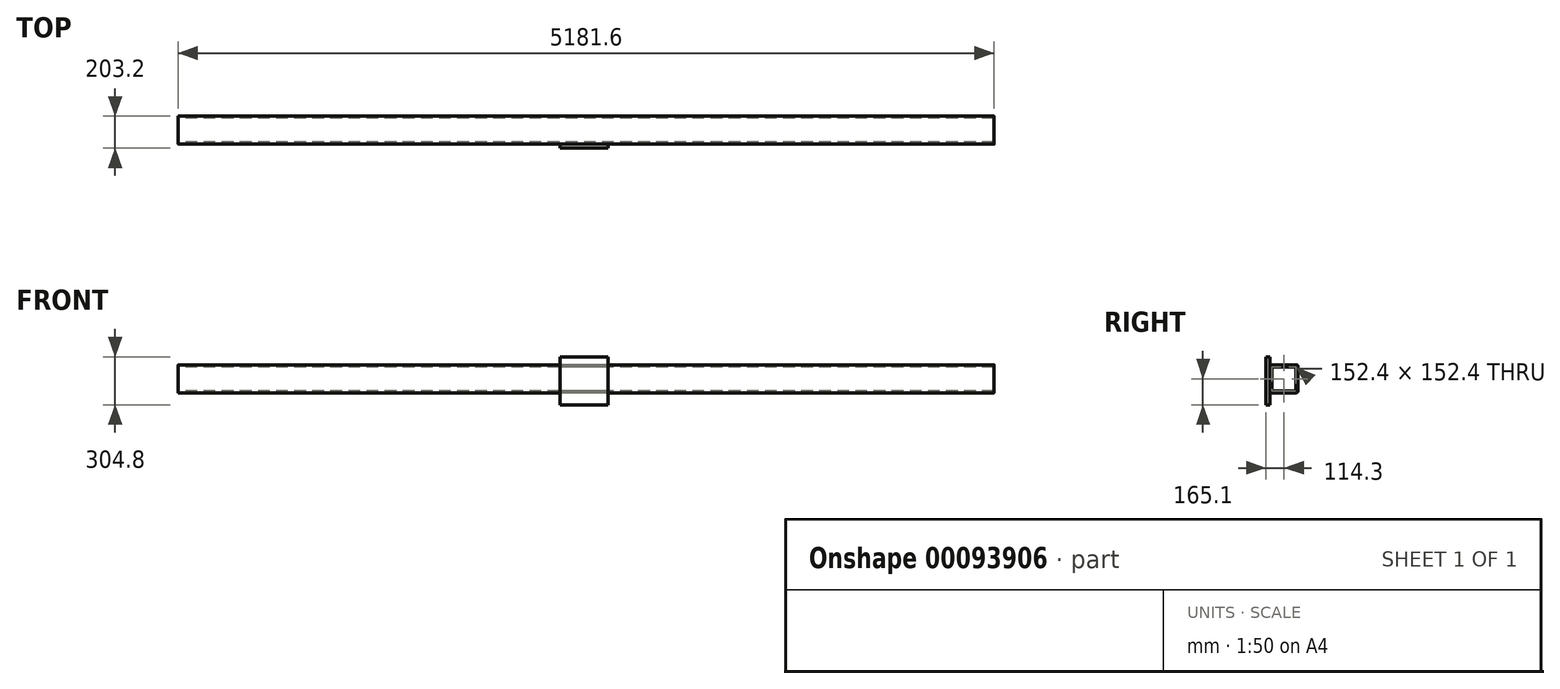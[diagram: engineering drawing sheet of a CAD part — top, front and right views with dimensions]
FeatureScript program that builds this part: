
annotation { "Feature Type Name" : "Feature", "Feature Type Description" : "" }
export const myFeature = defineFeature(function(context is Context, id is Id, definition is map)
    precondition{}
    {
        {
            var Q0;
            Q0=qCreatedBy(makeId("Right.planeOp"),FACE);
            var sketch = newSketch(context, id + "F0", { "sketchPlane" : qUnion([Q0])});
            skLineSegment(sketch, "E0.bottom", {"start": v(-76.2, 88.9) * mm, "end": v(76.2, 88.9) * mm});
            skLineSegment(sketch, "E0.top", {"start": v(-76.2, -88.9) * mm, "end": v(76.2, -88.9) * mm});
            skLineSegment(sketch, "E0.left", {"start": v(-88.9, 76.2) * mm, "end": v(-88.9, -76.2) * mm});
            skLineSegment(sketch, "E0.right", {"start": v(88.9, 76.2) * mm, "end": v(88.9, -76.2) * mm});
            skPoint(sketch, "E1.visualSharp", {"position": v(-88.9, 88.9) * mm});
            skArc(sketch, "E1.filletArc", {"start": v(-76.2, 88.9) * mm, "mid": v(-85.18, 85.18) * mm, "end": v(-88.9, 76.2) * mm});
            skPoint(sketch, "E2.visualSharp", {"position": v(88.9, 88.9) * mm});
            skArc(sketch, "E2.filletArc", {"start": v(88.9, 76.2) * mm, "mid": v(85.18, 85.18) * mm, "end": v(76.2, 88.9) * mm});
            skPoint(sketch, "E3.visualSharp", {"position": v(88.9, -88.9) * mm});
            skArc(sketch, "E3.filletArc", {"start": v(76.2, -88.9) * mm, "mid": v(85.18, -85.18) * mm, "end": v(88.9, -76.2) * mm});
            skPoint(sketch, "E4.visualSharp", {"position": v(-88.9, -88.9) * mm});
            skArc(sketch, "E4.filletArc", {"start": v(-88.9, -76.2) * mm, "mid": v(-85.18, -85.18) * mm, "end": v(-76.2, -88.9) * mm});
            skLineSegment(sketch, "E5.0", {"start": v(-76.2, 76.2) * mm, "end": v(-76.2, 76.2) * mm});
            skLineSegment(sketch, "E5.1", {"start": v(-76.2, 76.2) * mm, "end": v(76.2, 76.2) * mm});
            skLineSegment(sketch, "E5.2", {"start": v(-76.2, 76.2) * mm, "end": v(-76.2, -76.2) * mm});
            skLineSegment(sketch, "E5.3", {"start": v(76.2, 76.2) * mm, "end": v(76.2, 76.2) * mm});
            skLineSegment(sketch, "E5.4", {"start": v(-76.2, -76.2) * mm, "end": v(-76.2, -76.2) * mm});
            skLineSegment(sketch, "E5.5", {"start": v(-76.2, -76.2) * mm, "end": v(76.2, -76.2) * mm});
            skLineSegment(sketch, "E5.6", {"start": v(76.2, -76.2) * mm, "end": v(76.2, -76.2) * mm});
            skLineSegment(sketch, "E5.7", {"start": v(76.2, 76.2) * mm, "end": v(76.2, -76.2) * mm});
            skSolve(sketch);
        }
        {
            var Q0;
            Q0=makeQuery(id+"F0.imprint","IMPRINT",FACE,{"disambiguationData":[TD([[makeQuery(id+"F0.imprint","IMPRINT",EDGE,{"derivedFrom":sQuery(id+"F0.wireOp",EDGE,"E0.bottom")}),-1.0]])]});
            extrude(context, id + "F1", {"entities" : qUnion([Q0]), "endBound" : BoundingType.SYMMETRIC, "depth" : 5181.6 * mm});
        }
        {
            var Q0;
            Q0=makeQuery(id+"F1.opExtrude","SWEPT_FACE",FACE,{"disambiguationData":[OSD([sQuery(id+"F0.wireOp",EDGE,"E0.left")])]});
            var sketch = newSketch(context, id + "F2", { "sketchPlane" : qUnion([Q0])});
            skLineSegment(sketch, "E6.bottom", {"start": v(-166.5, 139.7) * mm, "end": v(138.3, 139.7) * mm});
            skLineSegment(sketch, "E6.top", {"start": v(-166.5, -165.1) * mm, "end": v(138.3, -165.1) * mm});
            skLineSegment(sketch, "E6.left", {"start": v(-166.5, 139.7) * mm, "end": v(-166.5, -165.1) * mm});
            skLineSegment(sketch, "E6.right", {"start": v(138.3, 139.7) * mm, "end": v(138.3, -165.1) * mm});
            skSolve(sketch);
        }
        {
            var Q0;
            Q0 = qSketchRegion(id + "F2", true);
            extrude(context, id + "F3", {"entities" : qUnion([Q0]), "operationType" : NewBodyOperationType.ADD, "depth" : 25.4 * mm, "offsetDistance" : 25.4 * mm});
        }
    });
